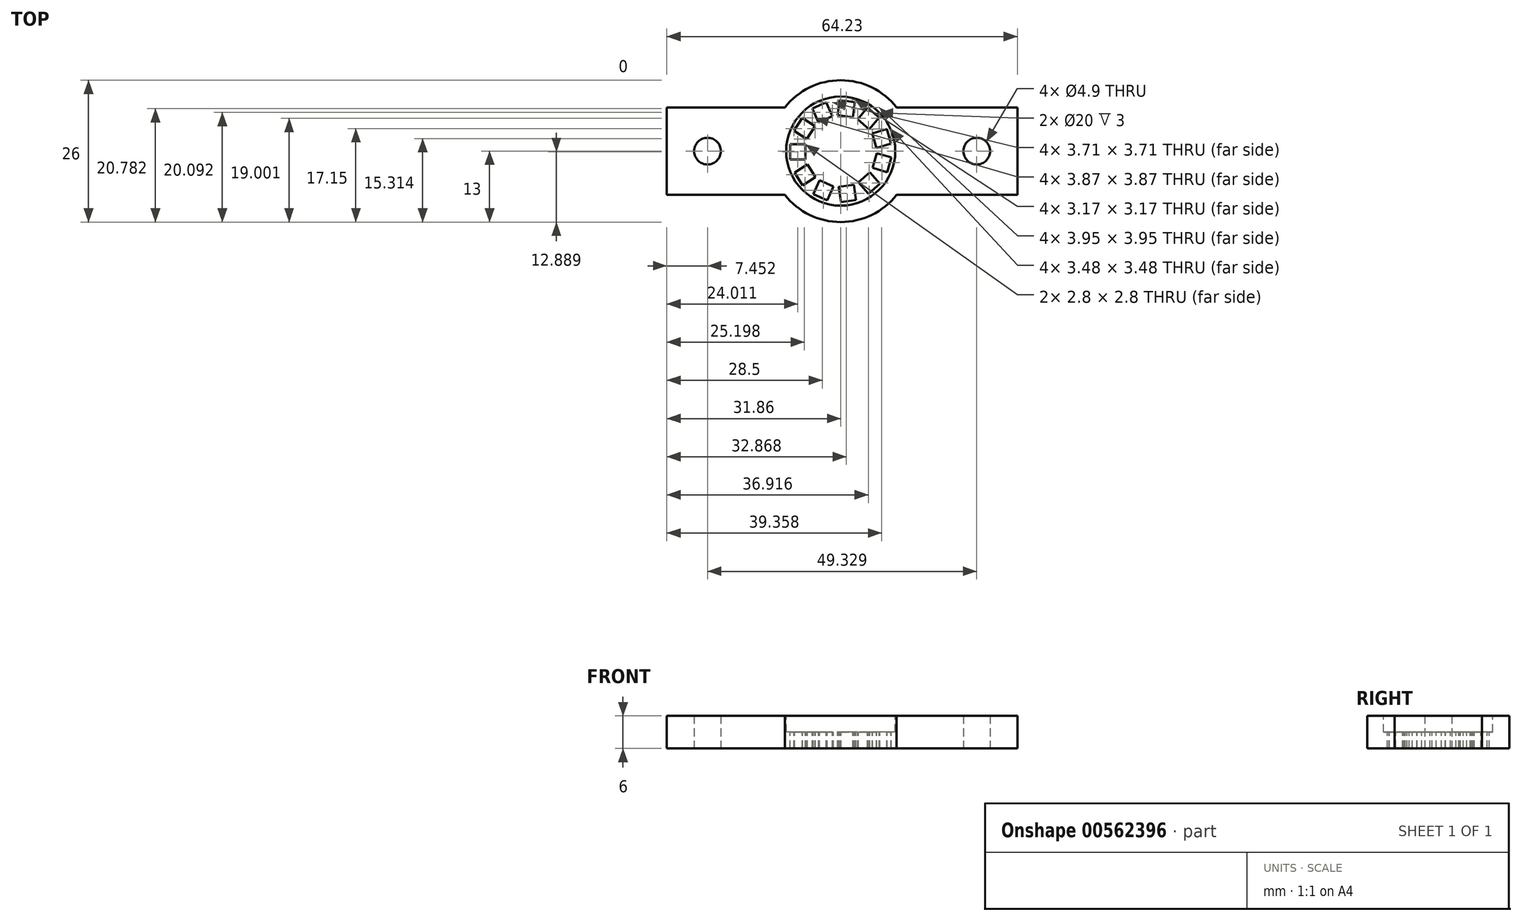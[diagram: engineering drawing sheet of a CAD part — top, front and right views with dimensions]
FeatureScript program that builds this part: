
annotation { "Feature Type Name" : "Feature", "Feature Type Description" : "" }
export const myFeature = defineFeature(function(context is Context, id is Id, definition is map)
    precondition{}
    {
        {
            var Q0;
            Q0=qCreatedBy(makeId("Top.planeOp"),FACE);
            var sketch = newSketch(context, id + "F0", { "sketchPlane" : qUnion([Q0])});
            skCircle(sketch, "E0", {"center": v(0, 0) * mm, "radius": 13 * mm});
            skLineSegment(sketch, "E1", {"start": v(10.25, 8) * mm, "end": v(32.37, 8) * mm});
            skLineSegment(sketch, "E2", {"start": v(32.37, 8) * mm, "end": v(32.37, -8) * mm});
            skLineSegment(sketch, "E3", {"start": v(32.37, -8) * mm, "end": v(10.25, -8) * mm});
            skCircle(sketch, "E4", {"center": v(24.92, 0) * mm, "radius": 2.45 * mm});
            skLineSegment(sketch, "E5", {"start": v(-10.25, -8) * mm, "end": v(-31.86, -8) * mm});
            skLineSegment(sketch, "E6", {"start": v(-31.86, -8) * mm, "end": v(-31.86, 8) * mm});
            skLineSegment(sketch, "E7", {"start": v(-31.86, 8) * mm, "end": v(-10.25, 8) * mm});
            skCircle(sketch, "E8", {"center": v(-24.4, 0) * mm, "radius": 2.45 * mm});
            skSolve(sketch);
        }
        {
            var Q0;
            Q0=qSketchRegion(id+"F0",true);
            extrude(context, id + "F1", {"entities" : qUnion([Q0]), "depth" : 6 * mm, "offsetDistance" : 25 * mm});
        }
        {
            var Q0;
            Q0=makeQuery(id+"F1.opExtrude","CAP_FACE",FACE,{"disambiguationData":[OSD([sQuery(id+"F0.wireOp",EDGE,"E0"),sQuery(id+"F0.wireOp",EDGE,"E1"),sQuery(id+"F0.wireOp",EDGE,"E2"),sQuery(id+"F0.wireOp",EDGE,"E3"),sQuery(id+"F0.wireOp",EDGE,"E4"),sQuery(id+"F0.wireOp",EDGE,"E5"),sQuery(id+"F0.wireOp",EDGE,"E6"),sQuery(id+"F0.wireOp",EDGE,"E7"),sQuery(id+"F0.wireOp",EDGE,"E8")])],"isStart":false});
            var sketch = newSketch(context, id + "F2", { "sketchPlane" : qUnion([Q0])});
            skCircle(sketch, "E9", {"center": v(0, 0) * mm, "radius": 10 * mm});
            skSolve(sketch);
        }
        {
            var Q0;
            Q0=makeQuery(id+"F2.imprint","IMPRINT",FACE,{"disambiguationData":[TD([[makeQuery(id+"F2.imprint","IMPRINT",EDGE,{"derivedFrom":sQuery(id+"F2.wireOp",EDGE,"E9")}),1.0]])]});
            extrude(context, id + "F3", {"entities" : qUnion([Q0]), "operationType" : NewBodyOperationType.REMOVE, "oppositeDirection" : true, "depth" : 3 * mm, "offsetDistance" : 25 * mm});
        }
        {
            var Q0;
            Q0=makeQuery(id+"F3.boolean.opBoolean","COPY",FACE,{"derivedFrom":makeQuery(id+"F3.opExtrude","CAP_FACE",FACE,{"disambiguationData":[OSD([sQuery(id+"F2.wireOp",EDGE,"E9")])],"isStart":false})});
            var sketch = newSketch(context, id + "F4", { "sketchPlane" : qUnion([Q0])});
            skLineSegment(sketch, "E10.bottom", {"start": v(-9.25, 1.29) * mm, "end": v(-6.45, 1.29) * mm});
            skLineSegment(sketch, "E10.top", {"start": v(-9.25, -1.51) * mm, "end": v(-6.45, -1.51) * mm});
            skLineSegment(sketch, "E10.left", {"start": v(-9.25, 1.29) * mm, "end": v(-9.25, -1.51) * mm});
            skLineSegment(sketch, "E10.right", {"start": v(-6.45, 1.29) * mm, "end": v(-6.45, -1.51) * mm});
            skLineSegment(sketch, "E11.1.0", {"start": v(-6.12, -2.4) * mm, "end": v(-4.6, -4.76) * mm});
            skLineSegment(sketch, "E11.1.1", {"start": v(-8.48, -3.92) * mm, "end": v(-6.12, -2.4) * mm});
            skLineSegment(sketch, "E11.1.2", {"start": v(-8.48, -3.92) * mm, "end": v(-6.96, -6.27) * mm});
            skLineSegment(sketch, "E11.1.3", {"start": v(-6.96, -6.27) * mm, "end": v(-4.6, -4.76) * mm});
            skLineSegment(sketch, "E11.2.0", {"start": v(-3.85, -5.33) * mm, "end": v(-1.3, -6.5) * mm});
            skLineSegment(sketch, "E11.2.1", {"start": v(-5.02, -7.88) * mm, "end": v(-3.85, -5.33) * mm});
            skLineSegment(sketch, "E11.2.2", {"start": v(-5.02, -7.88) * mm, "end": v(-2.47, -9.04) * mm});
            skLineSegment(sketch, "E11.2.3", {"start": v(-2.47, -9.04) * mm, "end": v(-1.3, -6.5) * mm});
            skLineSegment(sketch, "E11.3.0", {"start": v(-0.36, -6.57) * mm, "end": v(2.41, -6.17) * mm});
            skLineSegment(sketch, "E11.3.1", {"start": v(0.04, -9.34) * mm, "end": v(-0.36, -6.57) * mm});
            skLineSegment(sketch, "E11.3.2", {"start": v(0.04, -9.34) * mm, "end": v(2.8, -8.94) * mm});
            skLineSegment(sketch, "E11.3.3", {"start": v(2.8, -8.94) * mm, "end": v(2.41, -6.17) * mm});
            skLineSegment(sketch, "E11.4.0", {"start": v(3.25, -5.72) * mm, "end": v(5.36, -3.89) * mm});
            skLineSegment(sketch, "E11.4.1", {"start": v(5.08, -7.84) * mm, "end": v(3.25, -5.72) * mm});
            skLineSegment(sketch, "E11.4.2", {"start": v(5.08, -7.84) * mm, "end": v(7.2, -6) * mm});
            skLineSegment(sketch, "E11.4.3", {"start": v(7.2, -6) * mm, "end": v(5.36, -3.89) * mm});
            skLineSegment(sketch, "E11.5.0", {"start": v(5.82, -3.06) * mm, "end": v(6.61, -0.37) * mm});
            skLineSegment(sketch, "E11.5.1", {"start": v(8.5, -3.85) * mm, "end": v(5.82, -3.06) * mm});
            skLineSegment(sketch, "E11.5.2", {"start": v(8.5, -3.85) * mm, "end": v(9.3, -1.16) * mm});
            skLineSegment(sketch, "E11.5.3", {"start": v(9.3, -1.16) * mm, "end": v(6.61, -0.37) * mm});
            skLineSegment(sketch, "E11.6.0", {"start": v(6.55, 0.58) * mm, "end": v(5.76, 3.26) * mm});
            skLineSegment(sketch, "E11.6.1", {"start": v(9.24, 1.36) * mm, "end": v(6.55, 0.58) * mm});
            skLineSegment(sketch, "E11.6.2", {"start": v(9.24, 1.36) * mm, "end": v(8.45, 4.05) * mm});
            skLineSegment(sketch, "E11.6.3", {"start": v(8.45, 4.05) * mm, "end": v(5.76, 3.26) * mm});
            skLineSegment(sketch, "E11.7.0", {"start": v(5.2, 4.03) * mm, "end": v(3.08, 5.86) * mm});
            skLineSegment(sketch, "E11.7.1", {"start": v(7.03, 6.14) * mm, "end": v(5.2, 4.03) * mm});
            skLineSegment(sketch, "E11.7.2", {"start": v(7.03, 6.14) * mm, "end": v(4.92, 7.98) * mm});
            skLineSegment(sketch, "E11.7.3", {"start": v(4.92, 7.98) * mm, "end": v(3.08, 5.86) * mm});
            skLineSegment(sketch, "E11.8.0", {"start": v(2.2, 6.2) * mm, "end": v(-0.58, 6.6) * mm});
            skLineSegment(sketch, "E11.8.1", {"start": v(2.6, 8.97) * mm, "end": v(2.2, 6.2) * mm});
            skLineSegment(sketch, "E11.8.2", {"start": v(2.6, 8.97) * mm, "end": v(-0.18, 9.37) * mm});
            skLineSegment(sketch, "E11.8.3", {"start": v(-0.18, 9.37) * mm, "end": v(-0.58, 6.6) * mm});
            skLineSegment(sketch, "E11.9.0", {"start": v(-1.5, 6.4) * mm, "end": v(-4.05, 5.24) * mm});
            skLineSegment(sketch, "E11.9.1", {"start": v(-2.67, 8.95) * mm, "end": v(-1.5, 6.4) * mm});
            skLineSegment(sketch, "E11.9.2", {"start": v(-2.67, 8.95) * mm, "end": v(-5.21, 7.78) * mm});
            skLineSegment(sketch, "E11.9.3", {"start": v(-5.21, 7.78) * mm, "end": v(-4.05, 5.24) * mm});
            skLineSegment(sketch, "E11.10.0", {"start": v(-4.73, 4.57) * mm, "end": v(-6.24, 2.22) * mm});
            skLineSegment(sketch, "E11.10.1", {"start": v(-7.08, 6.08) * mm, "end": v(-4.73, 4.57) * mm});
            skLineSegment(sketch, "E11.10.2", {"start": v(-7.08, 6.08) * mm, "end": v(-8.6, 3.73) * mm});
            skLineSegment(sketch, "E11.10.3", {"start": v(-8.6, 3.73) * mm, "end": v(-6.24, 2.22) * mm});
            skPoint(sketch, "E11.center", {"position": v(0, 0) * mm});
            skSolve(sketch);
        }
        {
            var Q0;
            Q0=qSketchRegion(id+"F4",true);
            extrude(context, id + "F5", {"entities" : qUnion([Q0]), "operationType" : NewBodyOperationType.REMOVE, "endBound" : BoundingType.THROUGH_ALL, "oppositeDirection" : true, "depth" : 25 * mm, "offsetDistance" : 25 * mm});
        }
    });
